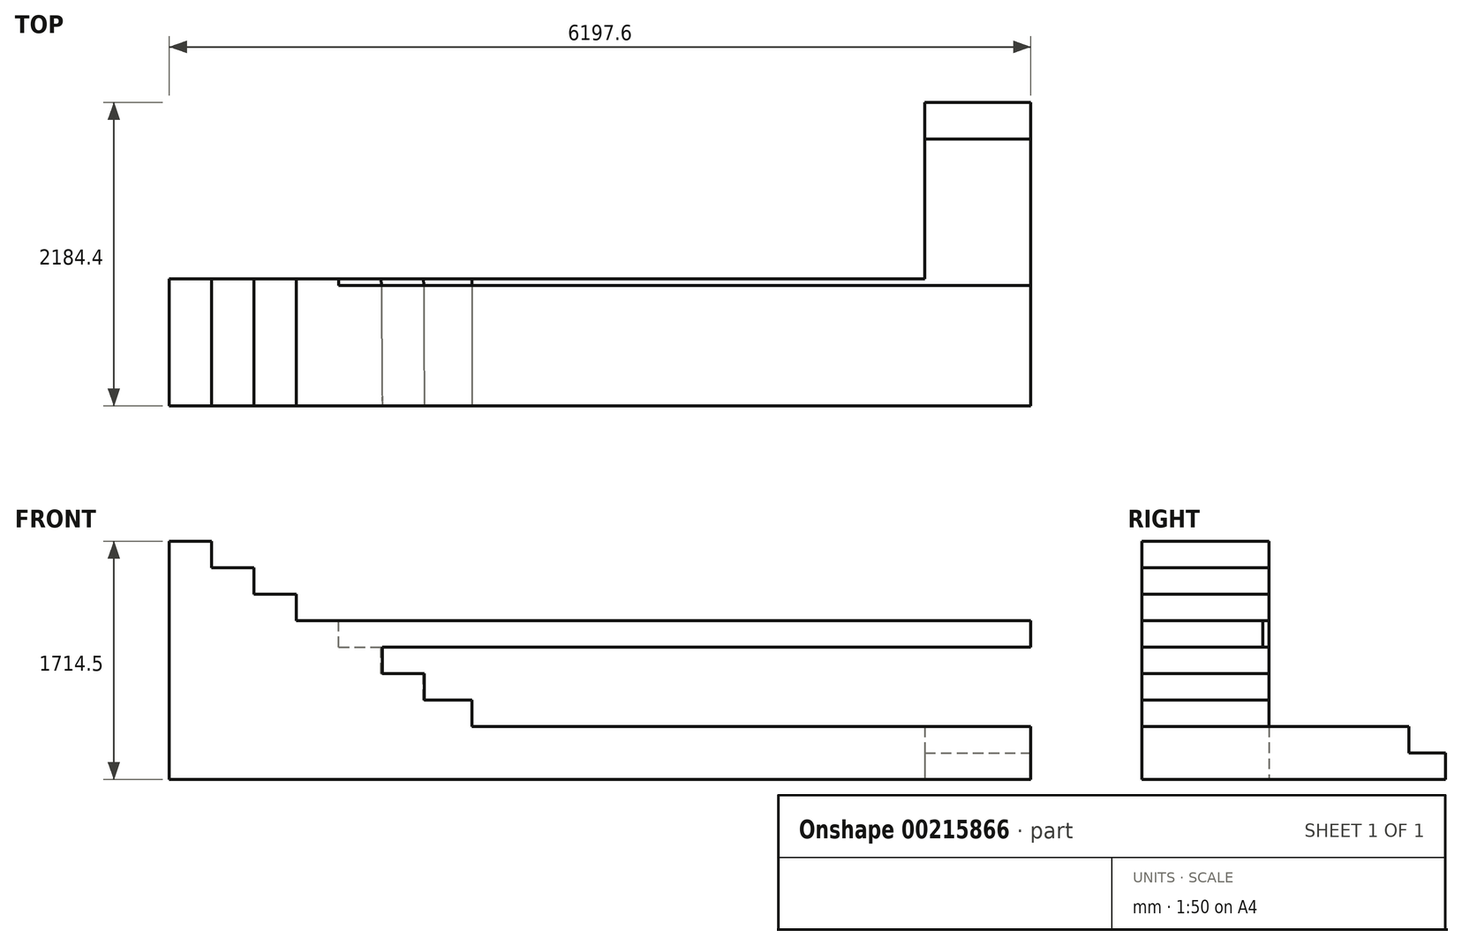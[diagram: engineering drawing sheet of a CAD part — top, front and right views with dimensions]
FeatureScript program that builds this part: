
annotation { "Feature Type Name" : "Feature", "Feature Type Description" : "" }
export const myFeature = defineFeature(function(context is Context, id is Id, definition is map)
    precondition{}
    {
        {
            var Q0;
            Q0=qCreatedBy(makeId("Top.planeOp"),FACE);
            var sketch = newSketch(context, id + "F0", { "sketchPlane" : qUnion([Q0])});
            skLineSegment(sketch, "E0", {"start": v(0, -1270) * mm, "end": v(0, -2184.4) * mm});
            skLineSegment(sketch, "E1", {"start": v(5435.6, 0) * mm, "end": v(6197.6, 0) * mm});
            skLineSegment(sketch, "E2", {"start": v(0, -1270) * mm, "end": v(5435.6, -1270) * mm});
            skLineSegment(sketch, "E3", {"start": v(5435.6, 0) * mm, "end": v(5435.6, -1270) * mm});
            skLineSegment(sketch, "E4", {"start": v(0, -2184.4) * mm, "end": v(6197.6, -2184.4) * mm});
            skLineSegment(sketch, "E5", {"start": v(6197.6, 0) * mm, "end": v(6197.6, -2184.4) * mm});
            skSolve(sketch);
        }
        {
            var Q0;
            Q0 = qSketchRegion(id + "F0", true);
            extrude(context, id + "F1", {"entities" : qUnion([Q0]), "depth" : 1714.5 * mm});
        }
        {
            var Q0;
            Q0=makeQuery(id+"F1.opExtrude","CAP_FACE",FACE,{"disambiguationData":[OSD([sQuery(id+"F0.wireOp",EDGE,"E0"),sQuery(id+"F0.wireOp",EDGE,"E1"),sQuery(id+"F0.wireOp",EDGE,"E2"),sQuery(id+"F0.wireOp",EDGE,"E3"),sQuery(id+"F0.wireOp",EDGE,"a2134479-14ab-4642-abb1-fb87a1dd6e02"),sQuery(id+"F0.wireOp",EDGE,"E4"),sQuery(id+"F0.wireOp",EDGE,"E5"),sQuery(id+"F0.wireOp",EDGE,"11dde14a-3c45-44b8-9611-408b0982c94f")])],"isStart":false});
            var sketch = newSketch(context, id + "F2", { "sketchPlane" : qUnion([Q0])});
            skLineSegment(sketch, "E6.bottom", {"start": v(304.8, 307.65) * mm, "end": v(7074.55, 307.65) * mm});
            skLineSegment(sketch, "E6.top", {"start": v(304.8, -2342.45) * mm, "end": v(7074.55, -2342.45) * mm});
            skLineSegment(sketch, "E6.left", {"start": v(304.8, 307.65) * mm, "end": v(304.8, -2342.45) * mm});
            skLineSegment(sketch, "E6.right", {"start": v(7074.55, 307.65) * mm, "end": v(7074.55, -2342.45) * mm});
            skSolve(sketch);
        }
        {
            var Q0;
            Q0 = qSketchRegion(id + "F2", true);
            extrude(context, id + "F3", {"entities" : qUnion([Q0]), "operationType" : NewBodyOperationType.REMOVE, "oppositeDirection" : true, "depth" : 190.5 * mm});
        }
        {
            var Q0;
            Q0=makeQuery(id+"F3.boolean.opBoolean","COPY",FACE,{"derivedFrom":makeQuery(id+"F3.opExtrude","CAP_FACE",FACE,{"disambiguationData":[OSD([sQuery(id+"F2.wireOp",EDGE,"E6.bottom"),sQuery(id+"F2.wireOp",EDGE,"E6.top"),sQuery(id+"F2.wireOp",EDGE,"E6.left"),sQuery(id+"F2.wireOp",EDGE,"E6.right")])],"isStart":false})});
            var sketch = newSketch(context, id + "F4", { "sketchPlane" : qUnion([Q0])});
            skLineSegment(sketch, "E7.bottom", {"start": v(609.6, 409.23) * mm, "end": v(6726.25, 409.23) * mm});
            skLineSegment(sketch, "E7.top", {"start": v(609.6, -2469.13) * mm, "end": v(6726.25, -2469.13) * mm});
            skLineSegment(sketch, "E7.left", {"start": v(609.6, 409.23) * mm, "end": v(609.6, -2469.13) * mm});
            skLineSegment(sketch, "E7.right", {"start": v(6726.25, 409.23) * mm, "end": v(6726.25, -2469.13) * mm});
            skSolve(sketch);
        }
        {
            var Q0;
            Q0 = qSketchRegion(id + "F4", true);
            extrude(context, id + "F5", {"entities" : qUnion([Q0]), "operationType" : NewBodyOperationType.REMOVE, "oppositeDirection" : true, "depth" : 190.5 * mm});
        }
        {
            var Q0;
            Q0=makeQuery(id+"F5.boolean.opBoolean","COPY",FACE,{"derivedFrom":makeQuery(id+"F5.opExtrude","CAP_FACE",FACE,{"disambiguationData":[OSD([sQuery(id+"F4.wireOp",EDGE,"E7.bottom"),sQuery(id+"F4.wireOp",EDGE,"E7.top"),sQuery(id+"F4.wireOp",EDGE,"E7.left"),sQuery(id+"F4.wireOp",EDGE,"E7.right")])],"isStart":false})});
            var sketch = newSketch(context, id + "F6", { "sketchPlane" : qUnion([Q0])});
            skLineSegment(sketch, "E8.bottom", {"start": v(914.4, 179.82) * mm, "end": v(6515.38, 179.82) * mm});
            skLineSegment(sketch, "E8.top", {"start": v(914.4, -2599.32) * mm, "end": v(6515.38, -2599.32) * mm});
            skLineSegment(sketch, "E8.left", {"start": v(914.4, 179.82) * mm, "end": v(914.4, -2599.32) * mm});
            skLineSegment(sketch, "E8.right", {"start": v(6515.38, 179.82) * mm, "end": v(6515.38, -2599.32) * mm});
            skSolve(sketch);
        }
        {
            var Q0;
            Q0 = qSketchRegion(id + "F6", true);
            extrude(context, id + "F7", {"entities" : qUnion([Q0]), "operationType" : NewBodyOperationType.REMOVE, "oppositeDirection" : true, "depth" : 190.5 * mm});
        }
        {
            var Q0;
            Q0=makeQuery(id+"F7.boolean.opBoolean","COPY",FACE,{"derivedFrom":makeQuery(id+"F7.opExtrude","CAP_FACE",FACE,{"disambiguationData":[OSD([sQuery(id+"F6.wireOp",EDGE,"E8.bottom"),sQuery(id+"F6.wireOp",EDGE,"E8.top"),sQuery(id+"F6.wireOp",EDGE,"E8.left"),sQuery(id+"F6.wireOp",EDGE,"E8.right")])],"isStart":false})});
            var sketch = newSketch(context, id + "F8", { "sketchPlane" : qUnion([Q0])});
            skLineSegment(sketch, "E9", {"start": v(1220.65, 1473.57) * mm, "end": v(1217.9, -1317.3) * mm});
            skLineSegment(sketch, "E10", {"start": v(1217.9, -1317.3) * mm, "end": v(6557.63, -1317.3) * mm});
            skLineSegment(sketch, "E11", {"start": v(6557.63, -1317.3) * mm, "end": v(6557.63, 1586.4) * mm});
            skLineSegment(sketch, "E12", {"start": v(6557.63, 1586.4) * mm, "end": v(1220.65, 1473.57) * mm});
            skPoint(sketch, "E13", {"position": v(1219.2, 0) * mm});
            skSolve(sketch);
        }
        {
            var Q0;
            Q0 = qSketchRegion(id + "F8", true);
            extrude(context, id + "F9", {"entities" : qUnion([Q0]), "operationType" : NewBodyOperationType.REMOVE, "oppositeDirection" : true, "depth" : 190.5 * mm});
        }
        {
            var Q0;
            Q0=makeQuery(id+"F9.boolean.opBoolean","COPY",FACE,{"derivedFrom":makeQuery(id+"F9.opExtrude","CAP_FACE",FACE,{"disambiguationData":[OSD([sQuery(id+"F8.wireOp",EDGE,"E9"),sQuery(id+"F8.wireOp",EDGE,"E10"),sQuery(id+"F8.wireOp",EDGE,"E11"),sQuery(id+"F8.wireOp",EDGE,"E12")])],"isStart":false})});
            var sketch = newSketch(context, id + "F10", { "sketchPlane" : qUnion([Q0])});
            skLineSegment(sketch, "E14", {"start": v(1512.74, 225.74) * mm, "end": v(1533.95, -2591.75) * mm});
            skLineSegment(sketch, "E15", {"start": v(1533.95, -2591.75) * mm, "end": v(7090.9, -2591.75) * mm});
            skLineSegment(sketch, "E16", {"start": v(7090.9, -2591.75) * mm, "end": v(6549.05, 597.08) * mm});
            skLineSegment(sketch, "E17", {"start": v(6549.05, 597.08) * mm, "end": v(1512.74, 225.74) * mm});
            skPoint(sketch, "E18", {"position": v(1524, -1270.33) * mm});
            skSolve(sketch);
        }
        {
            var Q0;
            Q0 = qSketchRegion(id + "F10", true);
            extrude(context, id + "F11", {"entities" : qUnion([Q0]), "operationType" : NewBodyOperationType.REMOVE, "oppositeDirection" : true, "depth" : 190.5 * mm});
        }
        {
            var Q0;
            Q0=makeQuery(id+"F11.boolean.opBoolean","COPY",FACE,{"derivedFrom":makeQuery(id+"F11.opExtrude","CAP_FACE",FACE,{"disambiguationData":[OSD([sQuery(id+"F10.wireOp",EDGE,"E14"),sQuery(id+"F10.wireOp",EDGE,"E15"),sQuery(id+"F10.wireOp",EDGE,"E16"),sQuery(id+"F10.wireOp",EDGE,"E17")])],"isStart":false})});
            var sketch = newSketch(context, id + "F12", { "sketchPlane" : qUnion([Q0])});
            skLineSegment(sketch, "E19", {"start": v(1822.2, 72.95) * mm, "end": v(1834.35, -2401.82) * mm});
            skLineSegment(sketch, "E20", {"start": v(1834.35, -2401.82) * mm, "end": v(6510.6, -2558.53) * mm});
            skLineSegment(sketch, "E21", {"start": v(6510.6, -2558.53) * mm, "end": v(6558.93, 203.4) * mm});
            skLineSegment(sketch, "E22", {"start": v(6558.93, 203.4) * mm, "end": v(1822.2, 72.95) * mm});
            skPoint(sketch, "E23", {"position": v(1828.8, -1269.83) * mm});
            skSolve(sketch);
        }
        {
            var Q0;
            Q0 = qSketchRegion(id + "F12", true);
            extrude(context, id + "F13", {"entities" : qUnion([Q0]), "operationType" : NewBodyOperationType.REMOVE, "oppositeDirection" : true, "depth" : 190.5 * mm});
        }
        {
            var Q0;
            Q0=makeQuery(id+"F13.boolean.opBoolean","COPY",FACE,{"derivedFrom":makeQuery(id+"F13.opExtrude","CAP_FACE",FACE,{"disambiguationData":[OSD([sQuery(id+"F12.wireOp",EDGE,"E19"),sQuery(id+"F12.wireOp",EDGE,"E20"),sQuery(id+"F12.wireOp",EDGE,"E21"),sQuery(id+"F12.wireOp",EDGE,"E22")])],"isStart":false})});
            var sketch = newSketch(context, id + "F14", { "sketchPlane" : qUnion([Q0])});
            skLineSegment(sketch, "E24.bottom", {"start": v(2178.03, 654.73) * mm, "end": v(6759.85, 654.73) * mm});
            skLineSegment(sketch, "E24.top", {"start": v(2178.03, -3309.64) * mm, "end": v(6759.85, -3309.64) * mm});
            skLineSegment(sketch, "E24.left", {"start": v(2178.03, 654.73) * mm, "end": v(2178.03, -3309.64) * mm});
            skLineSegment(sketch, "E24.right", {"start": v(6759.85, 654.73) * mm, "end": v(6759.85, -3309.64) * mm});
            skSolve(sketch);
        }
        {
            var Q0;
            Q0 = qSketchRegion(id + "F14", true);
            extrude(context, id + "F15", {"entities" : qUnion([Q0]), "operationType" : NewBodyOperationType.REMOVE, "oppositeDirection" : true, "depth" : 190.5 * mm});
        }
        {
            var Q0;
            Q0=makeQuery(id+"F15.boolean.opBoolean","COPY",FACE,{"derivedFrom":makeQuery(id+"F15.opExtrude","CAP_FACE",FACE,{"disambiguationData":[OSD([sQuery(id+"F14.wireOp",EDGE,"E24.bottom"),sQuery(id+"F14.wireOp",EDGE,"E24.top"),sQuery(id+"F14.wireOp",EDGE,"E24.left"),sQuery(id+"F14.wireOp",EDGE,"E24.right")])],"isStart":false})});
            var sketch = newSketch(context, id + "F16", { "sketchPlane" : qUnion([Q0])});
            skLineSegment(sketch, "E25.bottom", {"start": v(4057.25, 132.59) * mm, "end": v(6744.55, 132.59) * mm});
            skLineSegment(sketch, "E25.top", {"start": v(4057.25, -265.03) * mm, "end": v(6744.55, -265.03) * mm});
            skLineSegment(sketch, "E25.left", {"start": v(4057.25, 132.59) * mm, "end": v(4057.25, -265.03) * mm});
            skLineSegment(sketch, "E25.right", {"start": v(6744.55, 132.59) * mm, "end": v(6744.55, -265.03) * mm});
            skSolve(sketch);
        }
        {
            var Q0;
            Q0 = qSketchRegion(id + "F16", true);
            extrude(context, id + "F17", {"entities" : qUnion([Q0]), "operationType" : NewBodyOperationType.REMOVE, "oppositeDirection" : true, "depth" : 190.5 * mm});
        }
    });
